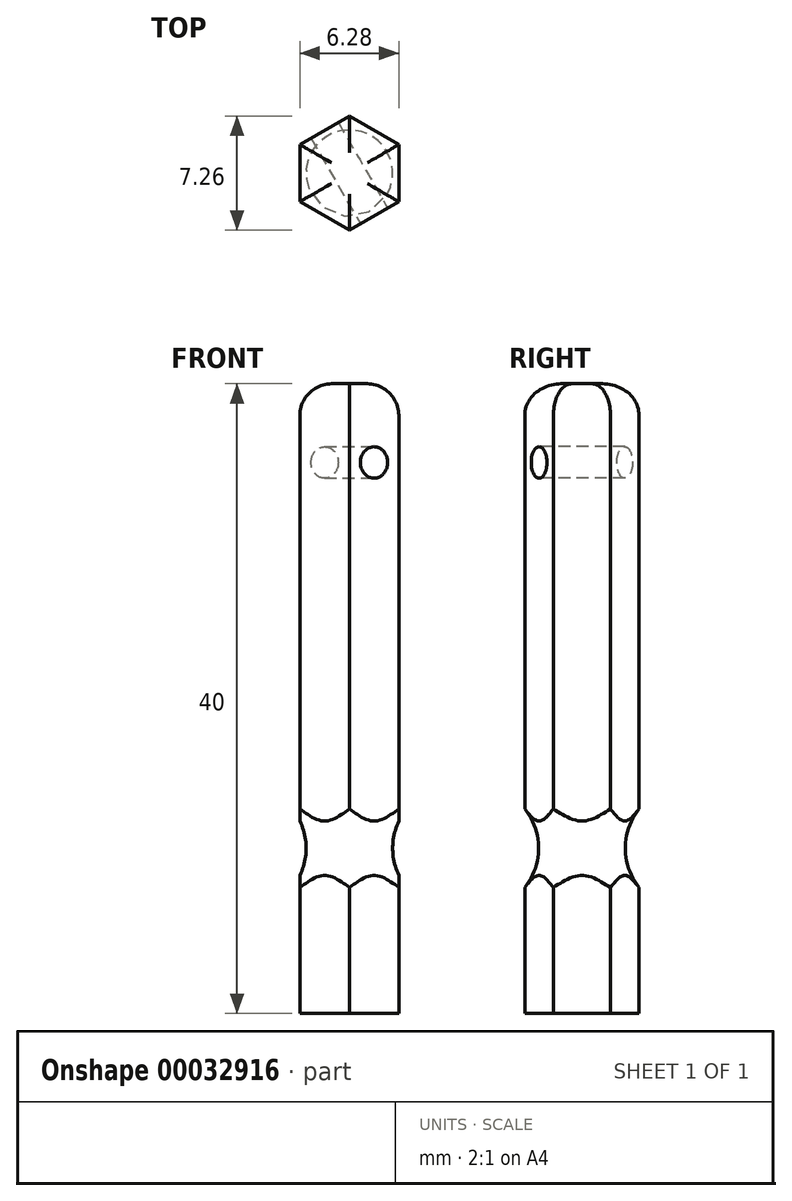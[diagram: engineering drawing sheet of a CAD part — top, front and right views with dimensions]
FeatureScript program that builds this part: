
annotation { "Feature Type Name" : "Feature", "Feature Type Description" : "" }
export const myFeature = defineFeature(function(context is Context, id is Id, definition is map)
    precondition{}
    {
        {
            var Q0;
            Q0=qCreatedBy(makeId("Top.planeOp"),FACE);
            var sketch = newSketch(context, id + "F0", { "sketchPlane" : qUnion([Q0])});
            skCircle(sketch, "E0.cCircle", {"center": v(0, 0) * mm, "radius": 3.14 * mm, "construction": true});
            skLineSegment(sketch, "E0.0", {"start": v(-3.14, 1.81) * mm, "end": v(0, 3.63) * mm});
            skLineSegment(sketch, "E0.1", {"start": v(0, 3.63) * mm, "end": v(3.14, 1.81) * mm});
            skLineSegment(sketch, "E0.2", {"start": v(3.14, 1.81) * mm, "end": v(3.14, -1.81) * mm});
            skLineSegment(sketch, "E0.3", {"start": v(3.14, -1.81) * mm, "end": v(0, -3.63) * mm});
            skLineSegment(sketch, "E0.4", {"start": v(0, -3.63) * mm, "end": v(-3.14, -1.81) * mm});
            skLineSegment(sketch, "E0.5", {"start": v(-3.14, -1.81) * mm, "end": v(-3.14, 1.81) * mm});
            skPoint(sketch, "E0.0.midPoint", {"position": v(-1.57, 2.72) * mm});
            skSolve(sketch);
        }
        {
            var Q0;
            Q0 = qSketchRegion(id + "F0", true);
            extrude(context, id + "F1", {"entities" : qUnion([Q0]), "depth" : 40 * mm});
        }
        {
            var Q0;
            Q0=makeQuery(id+"F1.opExtrude","SWEPT_FACE",FACE,{"disambiguationData":[OSD([sQuery(id+"F0.wireOp",EDGE,"E0.3")])]});
            var sketch = newSketch(context, id + "F2", { "sketchPlane" : qUnion([Q0])});
            skCircle(sketch, "E1", {"center": v(0, 35) * mm, "radius": 1 * mm});
            skSolve(sketch);
        }
        {
            var Q0;
            Q0 = qSketchRegion(id + "F2", true);
            extrude(context, id + "F3", {"entities" : qUnion([Q0]), "operationType" : NewBodyOperationType.REMOVE, "endBound" : BoundingType.THROUGH_ALL, "oppositeDirection" : true, "depth" : 25 * mm});
        }
        {
            var Q0;
            Q0=qCreatedBy(makeId("Top.planeOp"),FACE);
            cPlane(context, id + "F4", {"entities" : qUnion([Q0]), "cplaneType" : CPlaneType.OFFSET, "offset" : 10.5 * mm, "width" : 150 * mm, "height" : 150 * mm});
        }
        {
            var Q0;
            Q0=qCreatedBy(id+"F4.planeOp",FACE);
            var sketch = newSketch(context, id + "F5", { "sketchPlane" : qUnion([Q0])});
            skCircle(sketch, "E2", {"center": v(0, 0) * mm, "radius": 6.75 * mm});
            skSolve(sketch);
        }
        {
            var Q0;
            Q0=qCreatedBy(makeId("Front.planeOp"),FACE);
            var sketch = newSketch(context, id + "F6", { "sketchPlane" : qUnion([Q0])});
            skCircle(sketch, "E3", {"center": v(-6.75, 10.5) * mm, "radius": 4 * mm});
            skSolve(sketch);
        }
        {
            var Q0;
            Q0=makeQuery(id+"F6.imprint","IMPRINT",FACE,{"disambiguationData":[TD([[makeQuery(id+"F6.imprint","IMPRINT",EDGE,{"derivedFrom":sQuery(id+"F6.wireOp",EDGE,"E3")}),1.0]])]});
            var Q1;
            Q1=sQuery(id+"F5.wireOp",EDGE,"E2");
            sweep(context, id + "F7", {"operationType" : NewBodyOperationType.REMOVE, "profiles" : qUnion([Q0]), "path" : qUnion([Q1])});
        }
        {
            var Q0;
            Q0=makeQuery(id+"F1.opExtrude","CAP_EDGE",EDGE,{"disambiguationData":[OSD([sQuery(id+"F0.wireOp",EDGE,"E0.3")])],"isStart":false});
            var Q1;
            Q1=makeQuery(id+"F1.opExtrude","CAP_EDGE",EDGE,{"disambiguationData":[OSD([sQuery(id+"F0.wireOp",EDGE,"E0.4")])],"isStart":false});
            var Q2;
            Q2=makeQuery(id+"F1.opExtrude","CAP_EDGE",EDGE,{"disambiguationData":[OSD([sQuery(id+"F0.wireOp",EDGE,"E0.2")])],"isStart":false});
            var Q3;
            Q3=makeQuery(id+"F1.opExtrude","CAP_EDGE",EDGE,{"disambiguationData":[OSD([sQuery(id+"F0.wireOp",EDGE,"E0.0")])],"isStart":false});
            var Q4;
            Q4=makeQuery(id+"F1.opExtrude","CAP_EDGE",EDGE,{"disambiguationData":[OSD([sQuery(id+"F0.wireOp",EDGE,"E0.5")])],"isStart":false});
            var Q5;
            Q5=makeQuery(id+"F1.opExtrude","CAP_EDGE",EDGE,{"disambiguationData":[OSD([sQuery(id+"F0.wireOp",EDGE,"E0.1")])],"isStart":false});
            fillet(context, id + "F8", {"entities" : qUnion([Q0, Q1, Q2, Q3, Q4, Q5]), "radius" : 2 * mm, "tangentPropagation" : true, "allowEdgeOverflow" : false});
        }
    });
